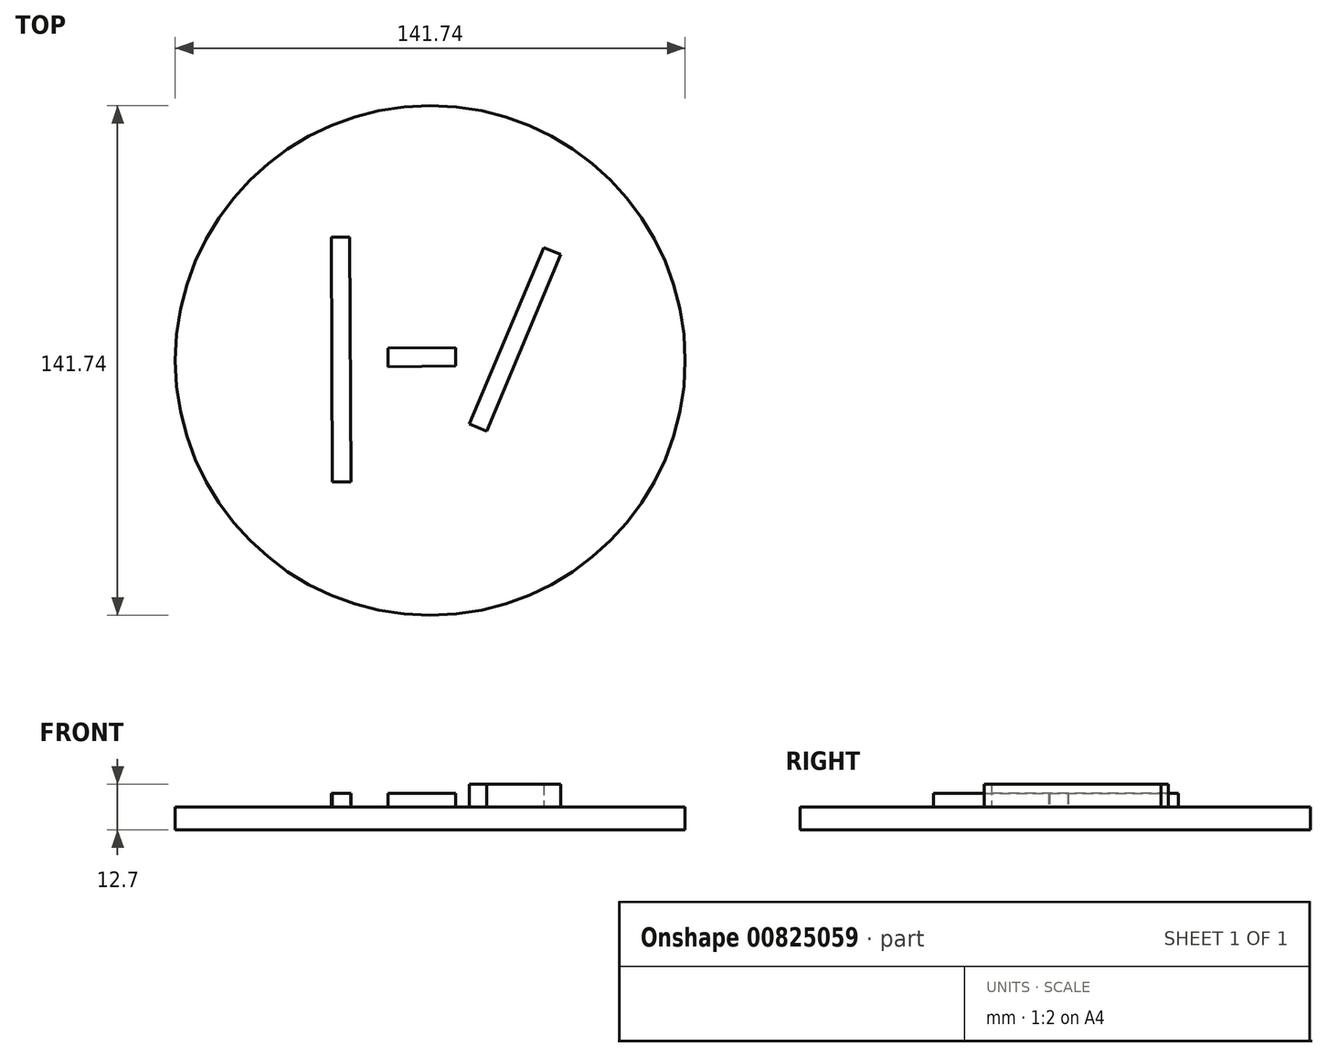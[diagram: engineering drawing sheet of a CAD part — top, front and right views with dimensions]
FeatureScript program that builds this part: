
annotation { "Feature Type Name" : "Feature", "Feature Type Description" : "" }
export const myFeature = defineFeature(function(context is Context, id is Id, definition is map)
    precondition{}
    {
        {
            var Q0;
            Q0=qCreatedBy(makeId("Top.planeOp"),FACE);
            var sketch = newSketch(context, id + "F0", { "sketchPlane" : qUnion([Q0])});
            skCircle(sketch, "E0", {"center": v(0, 0) * mm, "radius": 70.87 * mm});
            skLineSegment(sketch, "E1", {"start": v(-27.54, 34.27) * mm, "end": v(-22.41, 34.27) * mm});
            skLineSegment(sketch, "E2", {"start": v(-22.41, 34.27) * mm, "end": v(-22.01, -33.82) * mm});
            skLineSegment(sketch, "E3", {"start": v(-22.01, -33.82) * mm, "end": v(-27.2, -33.85) * mm});
            skLineSegment(sketch, "E4", {"start": v(-27.2, -33.85) * mm, "end": v(-27.54, 34.27) * mm});
            skLineSegment(sketch, "E5", {"start": v(7.04, 3.58) * mm, "end": v(7.04, -1.53) * mm});
            skLineSegment(sketch, "E6", {"start": v(7.04, -1.53) * mm, "end": v(-11.78, -1.8) * mm});
            skLineSegment(sketch, "E7", {"start": v(-11.78, -1.8) * mm, "end": v(-11.78, 3.47) * mm});
            skLineSegment(sketch, "E8", {"start": v(-11.78, 3.47) * mm, "end": v(7.04, 3.58) * mm});
            skLineSegment(sketch, "E9", {"start": v(31.55, 31.4) * mm, "end": v(36.25, 29.43) * mm});
            skLineSegment(sketch, "E10", {"start": v(36.25, 29.43) * mm, "end": v(15.74, -19.72) * mm});
            skLineSegment(sketch, "E11", {"start": v(15.74, -19.72) * mm, "end": v(10.87, -17.69) * mm});
            skLineSegment(sketch, "E12", {"start": v(10.87, -17.69) * mm, "end": v(31.55, 31.4) * mm});
            skSolve(sketch);
        }
        {
            var Q0;
            Q0=qSketchRegion(id+"F0",true);
            extrude(context, id + "F1", {"entities" : qUnion([Q0]), "depth" : 6.35 * mm, "offsetDistance" : 25.4 * mm});
        }
        {
            var Q0;
            Q0=makeQuery(id+"F0.imprint","IMPRINT",FACE,{"disambiguationData":[TD([[makeQuery(id+"F0.imprint","IMPRINT",EDGE,{"derivedFrom":sQuery(id+"F0.wireOp",EDGE,"E1")}),-1.0]])]});
            var Q1;
            Q1=makeQuery(id+"F0.imprint","IMPRINT",FACE,{"disambiguationData":[TD([[makeQuery(id+"F0.imprint","IMPRINT",EDGE,{"derivedFrom":sQuery(id+"F0.wireOp",EDGE,"E5")}),-1.0]])]});
            extrude(context, id + "F2", {"entities" : qUnion([Q0, Q1]), "operationType" : NewBodyOperationType.ADD, "depth" : 10.16 * mm, "offsetDistance" : 25.4 * mm});
        }
        {
            var Q0;
            Q0=makeQuery(id+"F0.imprint","IMPRINT",FACE,{"disambiguationData":[TD([[makeQuery(id+"F0.imprint","IMPRINT",EDGE,{"derivedFrom":sQuery(id+"F0.wireOp",EDGE,"E9")}),-1.0]])]});
            extrude(context, id + "F3", {"entities" : qUnion([Q0]), "operationType" : NewBodyOperationType.ADD, "depth" : 12.7 * mm, "offsetDistance" : 25.4 * mm});
        }
    });
